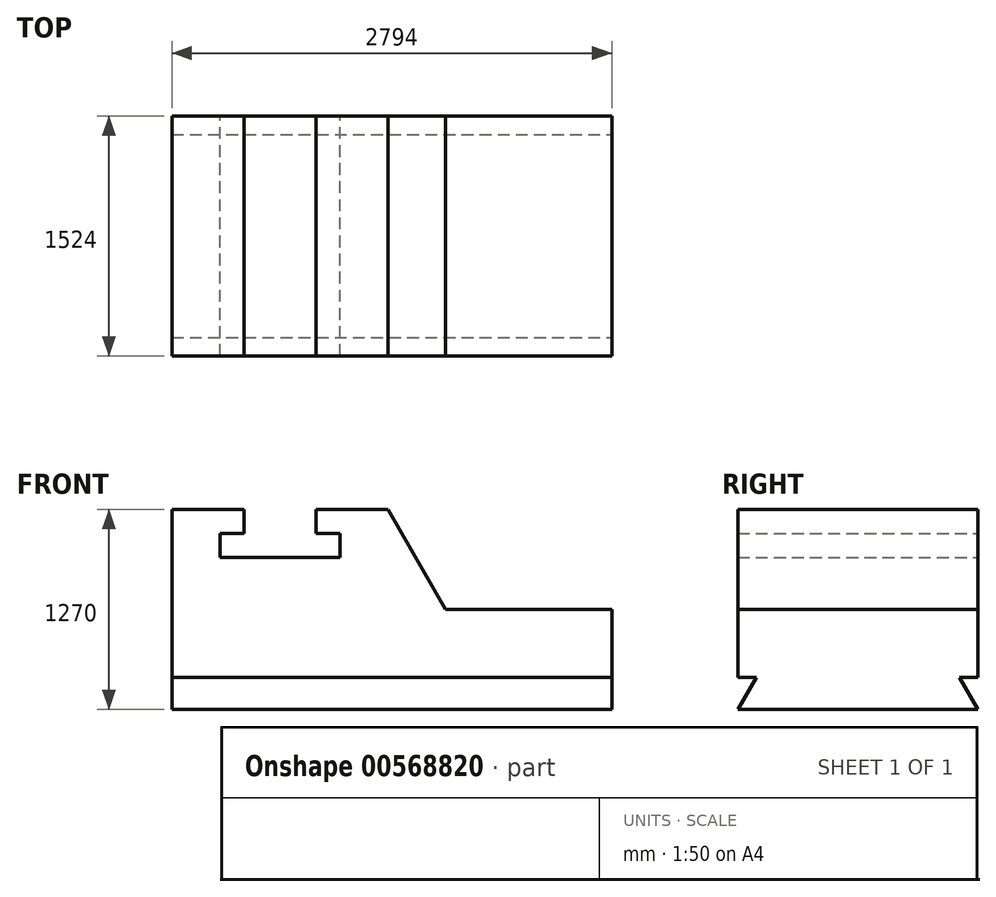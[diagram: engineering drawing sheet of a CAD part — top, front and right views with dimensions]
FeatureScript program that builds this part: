
annotation { "Feature Type Name" : "Feature", "Feature Type Description" : "" }
export const myFeature = defineFeature(function(context is Context, id is Id, definition is map)
    precondition{}
    {
        {
            var Q0;
            Q0=qCreatedBy(makeId("Top.planeOp"),FACE);
            var sketch = newSketch(context, id + "F0", { "sketchPlane" : qUnion([Q0])});
            skLineSegment(sketch, "E0.bottom", {"start": v(0, 0) * mm, "end": v(2794, 0) * mm});
            skLineSegment(sketch, "E0.top", {"start": v(0, 1524) * mm, "end": v(2794, 1524) * mm});
            skLineSegment(sketch, "E0.left", {"start": v(0, 0) * mm, "end": v(0, 1524) * mm});
            skLineSegment(sketch, "E0.right", {"start": v(2794, 0) * mm, "end": v(2794, 1524) * mm});
            skSolve(sketch);
        }
        {
            var Q0;
            Q0=makeQuery(id+"F0.imprint","IMPRINT",FACE,{"disambiguationData":[TD([[makeQuery(id+"F0.imprint","IMPRINT",EDGE,{"derivedFrom":sQuery(id+"F0.wireOp",EDGE,"E0.bottom")}),1.0]])]});
            extrude(context, id + "F1", {"entities" : qUnion([Q0]), "depth" : 635 * mm, "offsetDistance" : 25.4 * mm});
        }
        {
            var Q0;
            Q0=makeQuery(id+"F1.opExtrude","SWEPT_FACE",FACE,{"disambiguationData":[OSD([sQuery(id+"F0.wireOp",EDGE,"E0.right")])]});
            var sketch = newSketch(context, id + "F2", { "sketchPlane" : qUnion([Q0])});
            skLineSegment(sketch, "E1", {"start": v(0, 0) * mm, "end": v(0, 203.2) * mm});
            skLineSegment(sketch, "E2", {"start": v(0, 203.2) * mm, "end": v(117.32, 203.2) * mm});
            skLineSegment(sketch, "E3", {"start": v(117.32, 203.2) * mm, "end": v(0, 0) * mm});
            skSolve(sketch);
        }
        {
            var Q0;
            Q0=makeQuery(id+"F2.imprint","IMPRINT",FACE,{"disambiguationData":[TD([[makeQuery(id+"F2.imprint","IMPRINT",EDGE,{"derivedFrom":sQuery(id+"F2.wireOp",EDGE,"E1")}),1.0]])]});
            extrude(context, id + "F3", {"entities" : qUnion([Q0]), "operationType" : NewBodyOperationType.REMOVE, "endBound" : BoundingType.THROUGH_ALL, "oppositeDirection" : true, "depth" : 25.4 * mm, "offsetDistance" : 25.4 * mm});
        }
        {
            var Q0;
            Q0=makeQuery(id+"F1.opExtrude","SWEPT_FACE",FACE,{"disambiguationData":[OSD([sQuery(id+"F0.wireOp",EDGE,"E0.right")])]});
            var sketch = newSketch(context, id + "F4", { "sketchPlane" : qUnion([Q0])});
            skLineSegment(sketch, "E4", {"start": v(1524, 0) * mm, "end": v(1524, 203.2) * mm});
            skLineSegment(sketch, "E5", {"start": v(1524, 203.2) * mm, "end": v(1406.68, 203.2) * mm});
            skLineSegment(sketch, "E6", {"start": v(1406.68, 203.2) * mm, "end": v(1524, 0) * mm});
            skSolve(sketch);
        }
        {
            var Q0;
            Q0=makeQuery(id+"F4.imprint","IMPRINT",FACE,{"disambiguationData":[TD([[makeQuery(id+"F4.imprint","IMPRINT",EDGE,{"derivedFrom":sQuery(id+"F4.wireOp",EDGE,"E4")}),-1.0]])]});
            extrude(context, id + "F5", {"entities" : qUnion([Q0]), "operationType" : NewBodyOperationType.REMOVE, "endBound" : BoundingType.THROUGH_ALL, "oppositeDirection" : true, "depth" : 25.4 * mm, "offsetDistance" : 25.4 * mm});
        }
        {
            var Q0;
            Q0=makeQuery(id+"F1.opExtrude","SWEPT_FACE",FACE,{"disambiguationData":[OSD([sQuery(id+"F0.wireOp",EDGE,"E0.top")])]});
            var sketch = newSketch(context, id + "F6", { "sketchPlane" : qUnion([Q0])});
            skLineSegment(sketch, "E7", {"start": v(0, 635) * mm, "end": v(0, 1270) * mm});
            skLineSegment(sketch, "E8", {"start": v(0, 1270) * mm, "end": v(-457.2, 1270) * mm});
            skLineSegment(sketch, "E9", {"start": v(-457.2, 1270) * mm, "end": v(-457.2, 1117.6) * mm});
            skLineSegment(sketch, "E10", {"start": v(-457.2, 1117.6) * mm, "end": v(-304.8, 1117.6) * mm});
            skLineSegment(sketch, "E11", {"start": v(-304.8, 1117.6) * mm, "end": v(-304.8, 965.2) * mm});
            skLineSegment(sketch, "E12", {"start": v(-304.8, 965.2) * mm, "end": v(-1066.8, 965.2) * mm});
            skLineSegment(sketch, "E13", {"start": v(-1066.8, 965.2) * mm, "end": v(-1066.8, 1117.6) * mm});
            skLineSegment(sketch, "E14", {"start": v(-1066.8, 1117.6) * mm, "end": v(-914.4, 1117.6) * mm});
            skLineSegment(sketch, "E15", {"start": v(-914.4, 1117.6) * mm, "end": v(-914.4, 1270) * mm});
            skLineSegment(sketch, "E16", {"start": v(-914.4, 1270) * mm, "end": v(-1371.6, 1270) * mm});
            skLineSegment(sketch, "E17", {"start": v(-1371.6, 1270) * mm, "end": v(-1738.22, 635) * mm});
            skLineSegment(sketch, "E18", {"start": v(-1738.22, 635) * mm, "end": v(0, 635) * mm});
            skSolve(sketch);
        }
        {
            var Q0;
            Q0=makeQuery(id+"F6.imprint","IMPRINT",FACE,{"disambiguationData":[TD([[makeQuery(id+"F6.imprint","IMPRINT",EDGE,{"derivedFrom":sQuery(id+"F6.wireOp",EDGE,"E7")}),1.0]])]});
            extrude(context, id + "F7", {"entities" : qUnion([Q0]), "operationType" : NewBodyOperationType.ADD, "oppositeDirection" : true, "depth" : 1524 * mm, "offsetDistance" : 25.4 * mm});
        }
    });
